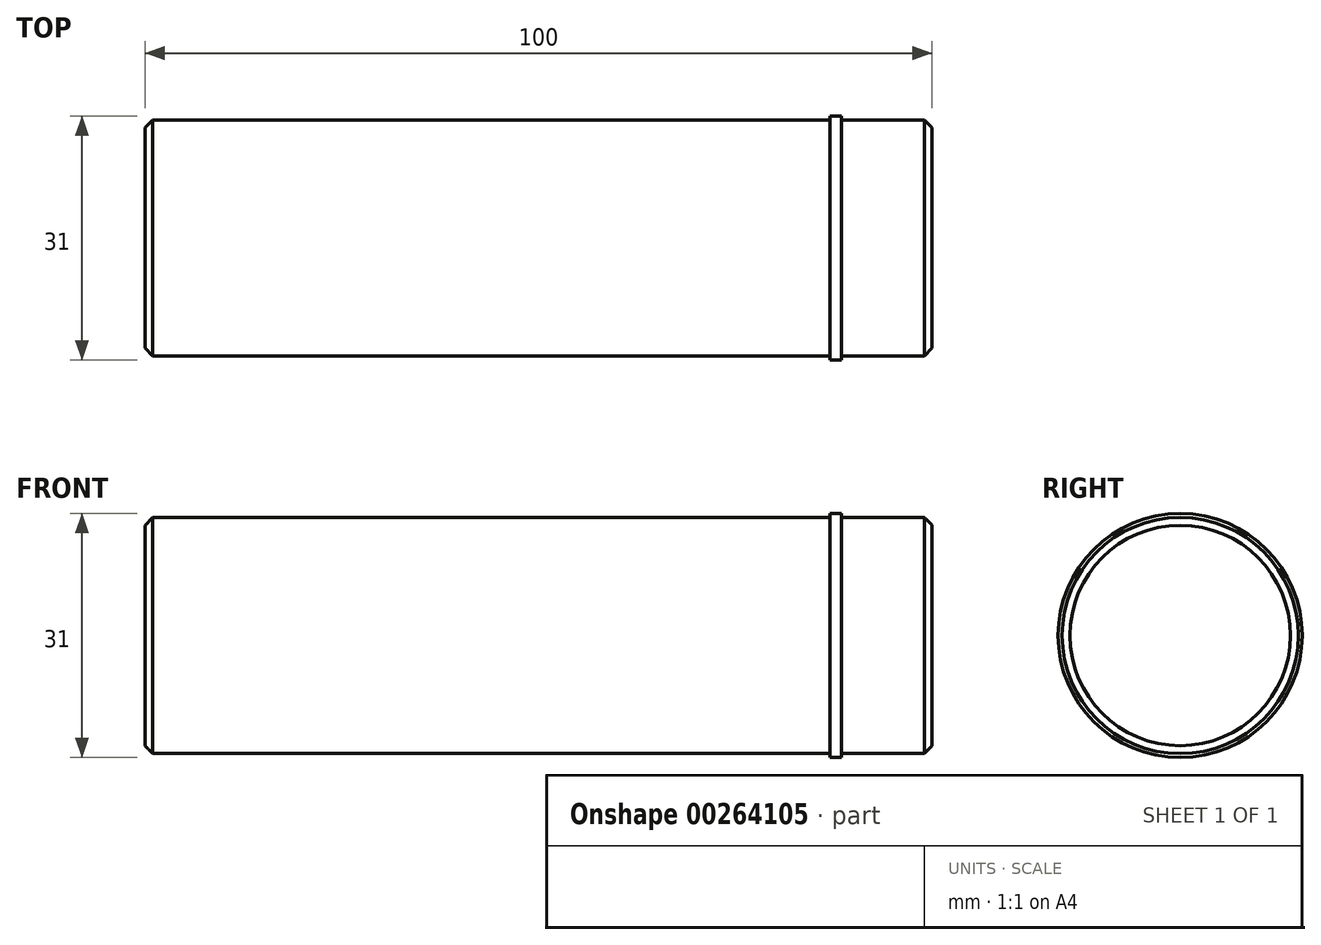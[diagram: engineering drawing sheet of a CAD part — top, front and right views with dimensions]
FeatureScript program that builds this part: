
annotation { "Feature Type Name" : "Feature", "Feature Type Description" : "" }
export const myFeature = defineFeature(function(context is Context, id is Id, definition is map)
    precondition{}
    {
        {
            var Q0;
            Q0=qCreatedBy(makeId("Front.planeOp"),FACE);
            var sketch = newSketch(context, id + "F0", { "sketchPlane" : qUnion([Q0])});
            skLineSegment(sketch, "E0", {"start": v(-50, 0) * mm, "end": v(50, 0) * mm});
            skLineSegment(sketch, "E1", {"start": v(50, 0) * mm, "end": v(50, 15) * mm});
            skLineSegment(sketch, "E2", {"start": v(50, 15) * mm, "end": v(38.5, 15) * mm});
            skLineSegment(sketch, "E3", {"start": v(37, 15) * mm, "end": v(37, 15.5) * mm});
            skLineSegment(sketch, "E4", {"start": v(38.5, 15.5) * mm, "end": v(37, 15.5) * mm});
            skLineSegment(sketch, "E5", {"start": v(38.5, 15.5) * mm, "end": v(38.5, 15) * mm});
            skLineSegment(sketch, "E6", {"start": v(37, 15) * mm, "end": v(-50, 15) * mm});
            skLineSegment(sketch, "E7", {"start": v(-50, 15) * mm, "end": v(-50, 0) * mm});
            skSolve(sketch);
        }
        {
            var Q0;
            Q0=makeQuery(id+"F0.imprint","IMPRINT",FACE,{"disambiguationData":[TD([[makeQuery(id+"F0.imprint","IMPRINT",EDGE,{"derivedFrom":sQuery(id+"F0.wireOp",EDGE,"E0")}),1.0]])]});
            var Q1;
            Q1=sQuery(id+"F0.wireOp",EDGE,"E0");
            revolve(context, id + "F1", {"entities" : qUnion([Q0]), "axis" : qUnion([Q1]), "revolveType" : RevolveType.FULL});
        }
        {
            var Q0;
            Q0=makeQuery(id+"F1.opRevolve","SWEPT_EDGE",EDGE,{"disambiguationData":[OSD([sQuery(id+"F0.wireOp",EDGE,"E1"),sQuery(id+"F0.wireOp",EDGE,"E2")])]});
            var Q1;
            Q1=makeQuery(id+"F1.opRevolve","SWEPT_EDGE",EDGE,{"disambiguationData":[OSD([sQuery(id+"F0.wireOp",EDGE,"E6"),sQuery(id+"F0.wireOp",EDGE,"E7")])]});
            chamfer(context, id + "F2", {"entities" : qUnion([Q0, Q1]), "width" : 1 * mm, "tangentPropagation" : true});
        }
    });
